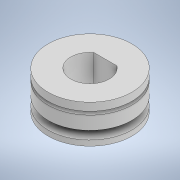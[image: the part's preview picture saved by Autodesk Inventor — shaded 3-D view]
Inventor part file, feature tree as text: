
AUTODESK INVENTOR PART (.ipt)
format: ipt  version: 2022.2 (Build 262287000, 287)  size: 146,944 bytes
history: native  units: mm
features: sketch x2, other x1, extrude x1, revolve x1
ambient origin geometry x8: Origin, YZ Plane, XZ Plane, XY Plane, X Axis, Y Axis, Z Axis, Center Point
bodies: Solid1 (feature_tree)
feature tree (5):
  other  "Motor.ipt"
  extrude  "Extrusion1"  Depth=10.0mm
  revolve  "Revolution1"  [1 undecoded]
  sketch  "Sketch1"  dims[d0=10.0mm d1=11.0mm]
  sketch  "Sketch2"  dims[d2=5.05mm d3=2.02mm d4=5.0mm d5=0.0mm d8=0.4mm d9=1.0mm d10=0.44mm d11=1.1mm d12=30.0deg d13=30.0deg d14=90.0deg]
note: 1 required parameter value undecoded (feature->parameter linkage not recoverable at this tier; creation-order binding heuristic only, values carry confidence <= 0.55)
